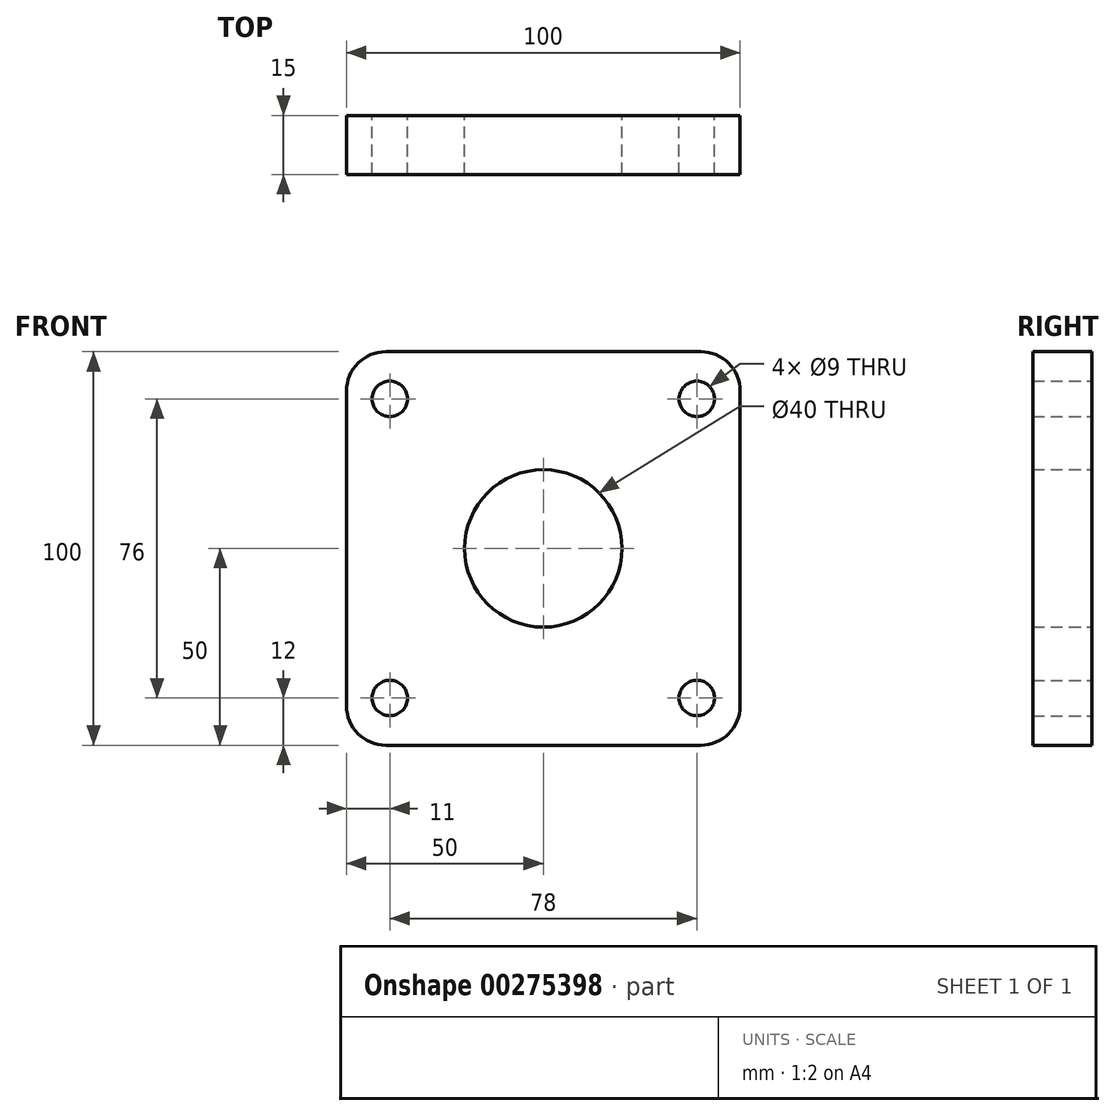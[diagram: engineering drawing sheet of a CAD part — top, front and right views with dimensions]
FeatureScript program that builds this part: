
annotation { "Feature Type Name" : "Feature", "Feature Type Description" : "" }
export const myFeature = defineFeature(function(context is Context, id is Id, definition is map)
    precondition{}
    {
        {
            var Q0;
            Q0=qCreatedBy(makeId("Front.planeOp"),FACE);
            var sketch = newSketch(context, id + "F0", { "sketchPlane" : qUnion([Q0])});
            skLineSegment(sketch, "E0.bottom", {"start": v(-40, 50) * mm, "end": v(40, 50) * mm});
            skLineSegment(sketch, "E0.top", {"start": v(-40, -50) * mm, "end": v(40, -50) * mm});
            skLineSegment(sketch, "E0.left", {"start": v(-50, 40) * mm, "end": v(-50, -40) * mm});
            skLineSegment(sketch, "E0.right", {"start": v(50, 40) * mm, "end": v(50, -40) * mm});
            skPoint(sketch, "E1.visualSharp", {"position": v(-50, 50) * mm});
            skArc(sketch, "E1.filletArc", {"start": v(-40, 50) * mm, "mid": v(-47.07, 47.07) * mm, "end": v(-50, 40) * mm});
            skPoint(sketch, "E2.visualSharp", {"position": v(50, 50) * mm});
            skArc(sketch, "E2.filletArc", {"start": v(50, 40) * mm, "mid": v(47.07, 47.07) * mm, "end": v(40, 50) * mm});
            skPoint(sketch, "E3.visualSharp", {"position": v(50, -50) * mm});
            skArc(sketch, "E3.filletArc", {"start": v(40, -50) * mm, "mid": v(47.07, -47.07) * mm, "end": v(50, -40) * mm});
            skPoint(sketch, "E4.visualSharp", {"position": v(-50, -50) * mm});
            skArc(sketch, "E4.filletArc", {"start": v(-50, -40) * mm, "mid": v(-47.07, -47.07) * mm, "end": v(-40, -50) * mm});
            skCircle(sketch, "E5", {"center": v(0, 0) * mm, "radius": 20 * mm});
            skCircle(sketch, "E6", {"center": v(-39, 38) * mm, "radius": 4.5 * mm});
            skCircle(sketch, "E7", {"center": v(-39, -38) * mm, "radius": 4.5 * mm});
            skCircle(sketch, "E8", {"center": v(39, 38) * mm, "radius": 4.5 * mm});
            skCircle(sketch, "E9", {"center": v(39, -38) * mm, "radius": 4.5 * mm});
            skSolve(sketch);
        }
        {
            var Q0;
            Q0=makeQuery(id+"F0.imprint","IMPRINT",FACE,{"disambiguationData":[TD([[makeQuery(id+"F0.imprint","IMPRINT",EDGE,{"derivedFrom":sQuery(id+"F0.wireOp",EDGE,"E0.bottom")}),-1.0]])]});
            extrude(context, id + "F1", {"entities" : qUnion([Q0]), "depth" : 15 * mm});
        }
    });
